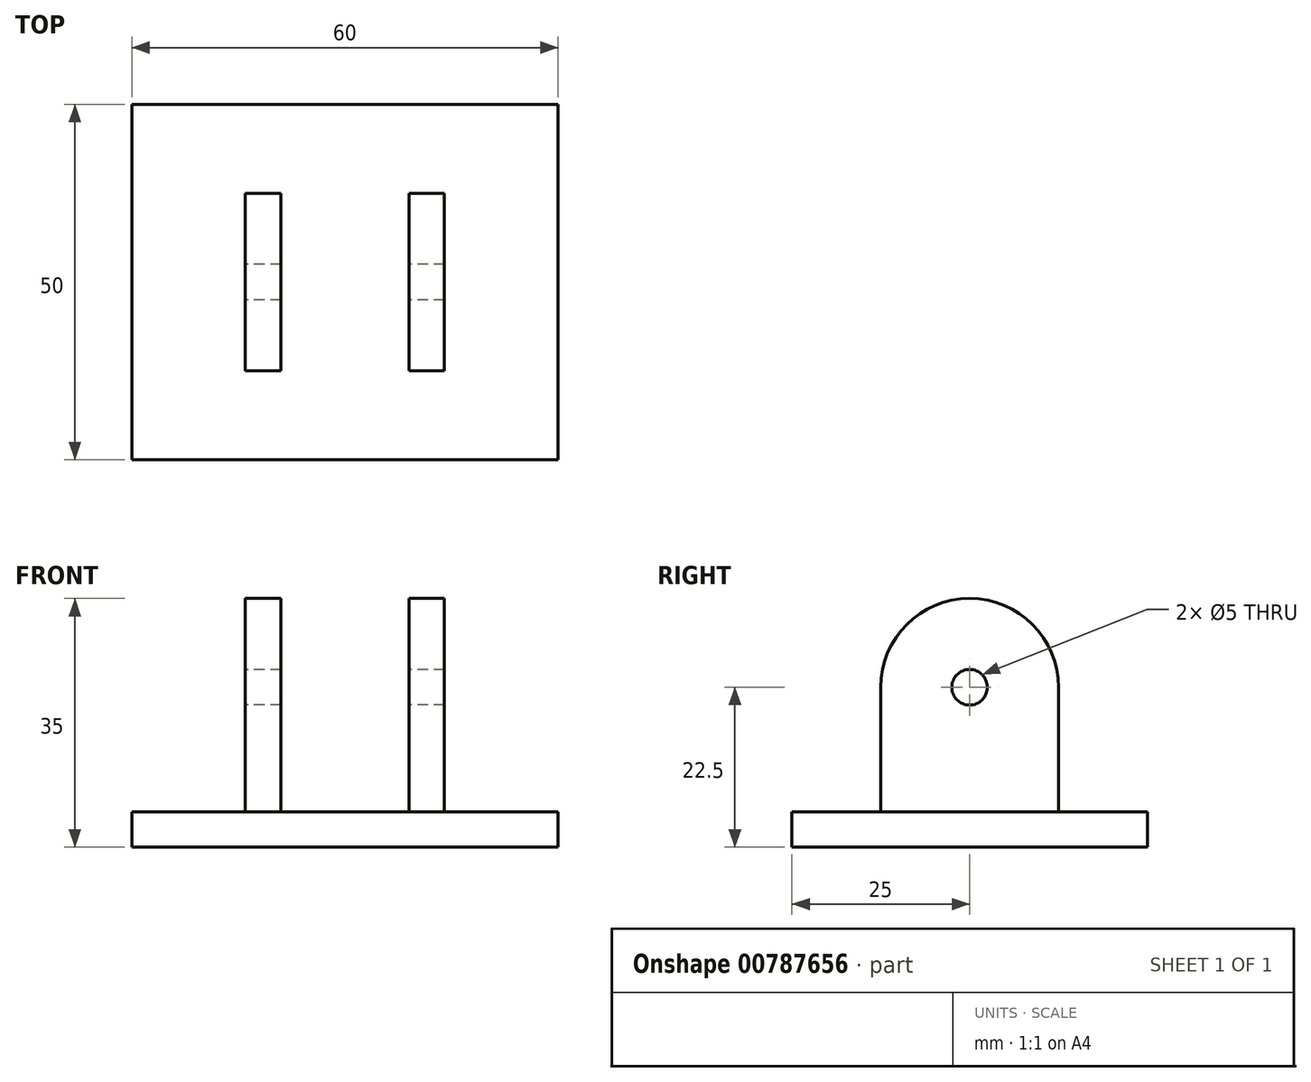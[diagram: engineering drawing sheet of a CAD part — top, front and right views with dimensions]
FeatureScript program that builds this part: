
annotation { "Feature Type Name" : "Feature", "Feature Type Description" : "" }
export const myFeature = defineFeature(function(context is Context, id is Id, definition is map)
    precondition{}
    {
        {
            var Q0;
            Q0=qCreatedBy(makeId("Top.planeOp"),FACE);
            var sketch = newSketch(context, id + "F0", { "sketchPlane" : qUnion([Q0])});
            skLineSegment(sketch, "E0.bottom", {"start": v(-30, 25) * mm, "end": v(30, 25) * mm});
            skLineSegment(sketch, "E0.top", {"start": v(-30, -25) * mm, "end": v(30, -25) * mm});
            skLineSegment(sketch, "E0.left", {"start": v(-30, 25) * mm, "end": v(-30, -25) * mm});
            skLineSegment(sketch, "E0.right", {"start": v(30, 25) * mm, "end": v(30, -25) * mm});
            skSolve(sketch);
        }
        {
            var Q0;
            Q0=makeQuery(id+"F0.imprint","IMPRINT",FACE,{"disambiguationData":[TD([[makeQuery(id+"F0.imprint","IMPRINT",EDGE,{"derivedFrom":sQuery(id+"F0.wireOp",EDGE,"E0.bottom")}),-1.0]])]});
            extrude(context, id + "F1", {"entities" : qUnion([Q0]), "depth" : 5 * mm, "offsetDistance" : 25 * mm});
        }
        {
            var Q0;
            Q0=makeQuery(id+"F1.opExtrude","CAP_FACE",FACE,{"disambiguationData":[OSD([sQuery(id+"F0.wireOp",EDGE,"E0.bottom"),sQuery(id+"F0.wireOp",EDGE,"E0.top"),sQuery(id+"F0.wireOp",EDGE,"E0.left"),sQuery(id+"F0.wireOp",EDGE,"E0.right")])],"isStart":false});
            var sketch = newSketch(context, id + "F2", { "sketchPlane" : qUnion([Q0])});
            skLineSegment(sketch, "E1.bottom", {"start": v(-14, 12.5) * mm, "end": v(-9, 12.5) * mm});
            skLineSegment(sketch, "E1.top", {"start": v(-14, -12.5) * mm, "end": v(-9, -12.5) * mm});
            skLineSegment(sketch, "E1.left", {"start": v(-14, 12.5) * mm, "end": v(-14, -12.5) * mm});
            skLineSegment(sketch, "E1.right", {"start": v(-9, 12.5) * mm, "end": v(-9, -12.5) * mm});
            skLineSegment(sketch, "E2.bottom", {"start": v(9, 12.5) * mm, "end": v(14, 12.5) * mm});
            skLineSegment(sketch, "E2.top", {"start": v(9, -12.5) * mm, "end": v(14, -12.5) * mm});
            skLineSegment(sketch, "E2.left", {"start": v(9, 12.5) * mm, "end": v(9, -12.5) * mm});
            skLineSegment(sketch, "E2.right", {"start": v(14, 12.5) * mm, "end": v(14, -12.5) * mm});
            skSolve(sketch);
        }
        {
            var Q0;
            Q0=makeQuery(id+"F2.imprint","IMPRINT",FACE,{"disambiguationData":[TD([[makeQuery(id+"F2.imprint","IMPRINT",EDGE,{"derivedFrom":sQuery(id+"F2.wireOp",EDGE,"E1.bottom")}),-1.0]])]});
            var Q1;
            Q1=makeQuery(id+"F2.imprint","IMPRINT",FACE,{"disambiguationData":[TD([[makeQuery(id+"F2.imprint","IMPRINT",EDGE,{"derivedFrom":sQuery(id+"F2.wireOp",EDGE,"E2.bottom")}),-1.0]])]});
            extrude(context, id + "F3", {"entities" : qUnion([Q0, Q1]), "operationType" : NewBodyOperationType.ADD, "depth" : 30 * mm, "offsetDistance" : 25 * mm});
        }
        {
            var Q0;
            Q0=makeQuery(id+"F3.opExtrude","CAP_EDGE",EDGE,{"disambiguationData":[OSD([sQuery(id+"F2.wireOp",EDGE,"E1.top")])],"isStart":false});
            var Q1;
            Q1=makeQuery(id+"F3.opExtrude","CAP_EDGE",EDGE,{"disambiguationData":[OSD([sQuery(id+"F2.wireOp",EDGE,"E1.bottom")])],"isStart":false});
            var Q2;
            Q2=makeQuery(id+"F3.opExtrude","CAP_EDGE",EDGE,{"disambiguationData":[OSD([sQuery(id+"F2.wireOp",EDGE,"E2.bottom")])],"isStart":false});
            var Q3;
            Q3=makeQuery(id+"F3.opExtrude","CAP_EDGE",EDGE,{"disambiguationData":[OSD([sQuery(id+"F2.wireOp",EDGE,"E2.top")])],"isStart":false});
            fillet(context, id + "F4", {"entities" : qUnion([Q0, Q1, Q2, Q3]), "radius" : 12.5 * mm, "tangentPropagation" : true, "allowEdgeOverflow" : false});
        }
        {
            var Q0;
            Q0=makeQuery(id+"F3.opExtrude","SWEPT_FACE",FACE,{"disambiguationData":[OSD([sQuery(id+"F2.wireOp",EDGE,"E1.left")])]});
            var sketch = newSketch(context, id + "F5", { "sketchPlane" : qUnion([Q0])});
            skCircle(sketch, "E3", {"center": v(0, 22.5) * mm, "radius": 2.5 * mm});
            skSolve(sketch);
        }
        {
            var Q0;
            Q0=makeQuery(id+"F5.imprint","IMPRINT",FACE,{"disambiguationData":[TD([[makeQuery(id+"F5.imprint","IMPRINT",EDGE,{"derivedFrom":sQuery(id+"F5.wireOp",EDGE,"E3")}),1.0]])]});
            extrude(context, id + "F6", {"entities" : qUnion([Q0]), "operationType" : NewBodyOperationType.REMOVE, "oppositeDirection" : true, "depth" : 50 * mm, "offsetDistance" : 25 * mm});
        }
    });
